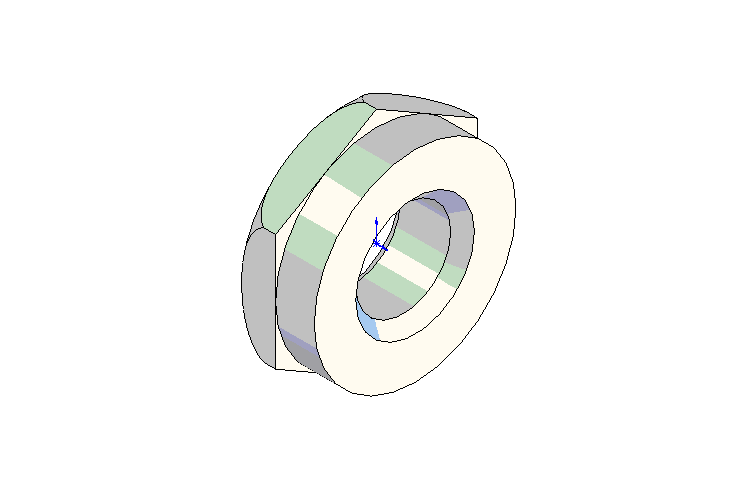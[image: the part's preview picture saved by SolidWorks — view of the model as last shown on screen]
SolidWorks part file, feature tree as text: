
SOLIDWORKS PART (.sldprt)
format: sldprt  version: not decoded by parser v0  size: 217,600 bytes
history: native  units: mm
features: plane x3, sketch x3, material x1, extrude x1, cut_extrude x1, cut_revolve x1, chamfer x1 (+10 scaffold rows collapsed)
feature tree (21):
  scaffold x10  (default folders/planes/origin — collapsed)
  material  "Matériau <non spécifié>"
  plane  "Plan de face"
  plane  "Plan de dessus"
  plane  "Plan de droite"
  sketch  "Esquisse2"  dims[D2=8.0mm D1=17.0mm]
  extrude  "Extrusion1"  Depth=3.25mm
  sketch  "Esquisse3"
  cut_extrude  "Enlèv. mat.-Extru.1"  [1 undecoded]
  sketch  "Esquisse4"  dims[D3=3.0mm D1=2.0mm D2=16.5mm]
  cut_revolve  "Enlèvement de matière-Révolution1"  Angle=360deg
  chamfer  "Chanfrein1"  Distance=1mm Angle=45deg
decode coverage: 5 of 7 modeling features carry decoded parameters
note: 1 parameter value undecoded
note: suppression state not decoded; provenance and decode notes live in map.json
